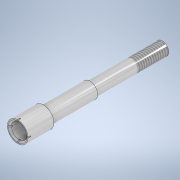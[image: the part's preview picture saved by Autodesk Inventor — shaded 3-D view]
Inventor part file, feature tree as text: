
AUTODESK INVENTOR PART (.ipt)
format: ipt  version: 2022 (Build 260153000, 153)  size: 171,520 bytes
history: native  units: mm
features: sketch x2, revolve x1, extrude x1, chamfer x1, thread x1
ambient origin geometry x8: Origin, YZ Plane, XZ Plane, XY Plane, X Axis, Y Axis, Z Axis, Center Point
bodies: Solid1 (feature_tree)
feature tree (6):
  revolve  "Revolution1"  [1 undecoded]
  extrude  "Extrusion1"  Depth=2.0mm
  chamfer  "Chamfer1"  Distance=1.25mm
  thread  "Thread1"  [1 undecoded]
  sketch  "Sketch1"  dims[d0=28.0mm d2=5.0mm]
  sketch  "Sketch2"  dims[d5=9.0mm d6=3.0mm d7=1.25mm d9=90.0deg d10=0.1mm d11=0.1mm d12=0.1mm d13=0.2mm d14=0.1mm d15=0.1mm d16=0.5mm d17=0.0mm d18=0.3mm d19=2.0mm d20=45.0deg d21=6.0mm d22=8.0mm d23=4.0mm d24=0.5mm]
note: 2 required parameter values undecoded (feature->parameter linkage not recoverable at this tier; creation-order binding heuristic only, values carry confidence <= 0.55)